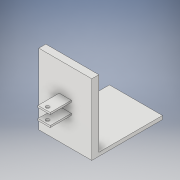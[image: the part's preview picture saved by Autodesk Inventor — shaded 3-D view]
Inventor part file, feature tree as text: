
AUTODESK INVENTOR PART (.ipt)
format: ipt  version: 2018 (Build 220112000, 112)  size: 135,168 bytes
history: native  units: in
note: dims shown in document units (in); Inventor stores cm internally (conversion verified against a paired STEP export)
features: extrude x5, sketch x5
ambient origin geometry x8: Origin, YZ Plane, XZ Plane, XY Plane, X Axis, Y Axis, Z Axis, Center Point
bodies: Solid1 (feature_tree)
feature tree (10):
  extrude  "Extrusion1"  Depth=10.0in
  extrude  "Extrusion2"  Depth=3.0in TaperAngle=0.0deg
  extrude  "Extrusion3"  Depth=3.0in TaperAngle=0.0deg
  extrude  "Extrusion4"  Depth=9.0in TaperAngle=0.0deg
  extrude  "Extrusion5"  Depth=1.738in
  sketch  "Sketch1"  dims[d0=7.5in d1=10.0in]
  sketch  "Sketch2"  dims[d2=1.0in d3=0.0in d8=3.0in d9=0.0in]
  sketch  "Sketch3"  dims[d10=0.5in d11=3.0in d12=0.0in]
  sketch  "Sketch4"  dims[d13=0.5in d14=9.0in d15=0.0in]
  sketch  "Sketch5"  dims[d16=0.869in d17=1.738in d18=0.25in d19=0.25in d20=0.5in d21=4.0in d22=0.0in]
